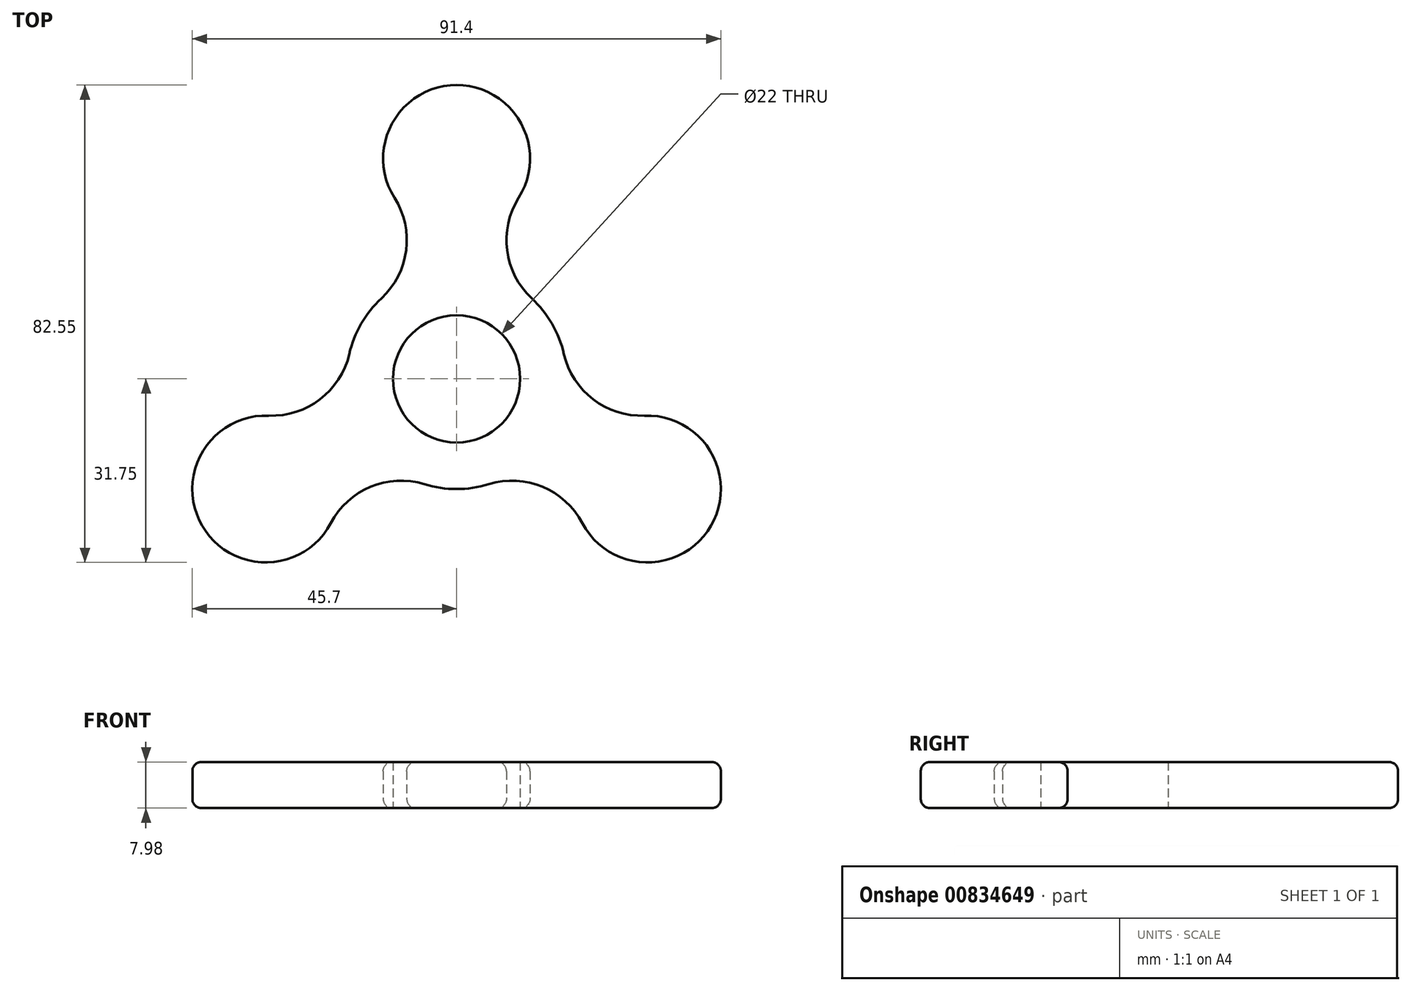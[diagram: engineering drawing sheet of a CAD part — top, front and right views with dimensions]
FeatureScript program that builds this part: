
annotation { "Feature Type Name" : "Feature", "Feature Type Description" : "" }
export const myFeature = defineFeature(function(context is Context, id is Id, definition is map)
    precondition{}
    {
        {
            var Q0;
            Q0=qCreatedBy(makeId("Top.planeOp"),FACE);
            var sketch = newSketch(context, id + "F0", { "sketchPlane" : qUnion([Q0])});
            skCircle(sketch, "E0", {"center": v(0, 0) * mm, "radius": 11 * mm});
            skLineSegment(sketch, "E1", {"start": v(0, 0) * mm, "end": v(0, 54.19) * mm, "construction": true});
            skLineSegment(sketch, "E2", {"start": v(0, 0) * mm, "end": v(61.7, 0) * mm, "construction": true});
            skCircle(sketch, "E3", {"center": v(0, 0) * mm, "radius": 19.05 * mm});
            skSolve(sketch);
        }
        {
            var Q0;
            Q0=qSketchRegion(id+"F0",true);
            extrude(context, id + "F1", {"entities" : qUnion([Q0]), "depth" : 7.98 * mm, "offsetDistance" : 25.4 * mm});
        }
        {
            var Q0;
            Q0=qCreatedBy(makeId("Top.planeOp"),FACE);
            var sketch = newSketch(context, id + "F2", { "sketchPlane" : qUnion([Q0])});
            skArc(sketch, "E4", {"start": v(10.74, 31.32) * mm, "mid": v(0, 50.8) * mm, "end": v(-10.74, 31.32) * mm});
            skArc(sketch, "E5", {"start": v(-13, 13.93) * mm, "mid": v(-8.73, 22.22) * mm, "end": v(-10.74, 31.32) * mm});
            skLineSegment(sketch, "E6", {"start": v(0, 38.1) * mm, "end": v(0, 0) * mm, "construction": true});
            skArc(sketch, "E7.MirrorCS", {"start": v(13, 13.93) * mm, "mid": v(8.73, 22.22) * mm, "end": v(10.74, 31.32) * mm});
            skLineSegment(sketch, "E8", {"start": v(-13, 13.93) * mm, "end": v(13, 13.93) * mm});
            skArc(sketch, "E9.1.0", {"start": v(-5.57, -18.22) * mm, "mid": v(-14.88, -18.68) * mm, "end": v(-21.76, -24.96) * mm});
            skLineSegment(sketch, "E9.1.1", {"start": v(-5.57, -18.22) * mm, "end": v(-18.56, 4.29) * mm});
            skArc(sketch, "E9.1.2", {"start": v(-32.5, -6.36) * mm, "mid": v(-44, -25.4) * mm, "end": v(-21.76, -24.96) * mm});
            skArc(sketch, "E9.1.3", {"start": v(-18.56, 4.29) * mm, "mid": v(-23.61, -3.55) * mm, "end": v(-32.5, -6.36) * mm});
            skArc(sketch, "E9.2.0", {"start": v(18.56, 4.29) * mm, "mid": v(23.61, -3.55) * mm, "end": v(32.5, -6.36) * mm});
            skLineSegment(sketch, "E9.2.1", {"start": v(18.56, 4.29) * mm, "end": v(5.57, -18.22) * mm});
            skArc(sketch, "E9.2.2", {"start": v(21.76, -24.96) * mm, "mid": v(44, -25.4) * mm, "end": v(32.5, -6.36) * mm});
            skArc(sketch, "E9.2.3", {"start": v(5.57, -18.22) * mm, "mid": v(14.88, -18.68) * mm, "end": v(21.76, -24.96) * mm});
            skPoint(sketch, "E9.center", {"position": v(0, 0) * mm});
            skSolve(sketch);
        }
        {
            var Q0;
            Q0 = qSketchRegion(id + "F2", true);
            extrude(context, id + "F3", {"entities" : qUnion([Q0]), "operationType" : NewBodyOperationType.ADD, "depth" : 7.98 * mm, "offsetDistance" : 25.4 * mm});
        }
        {
            var Q0;
            Q0=makeQuery(id+"F3.opExtrude","CAP_EDGE",EDGE,{"disambiguationData":[OSD([sQuery(id+"F2.wireOp",EDGE,"E9.1.0")])],"isStart":false});
            var Q1;
            Q1=makeQuery(id+"F3.opExtrude","CAP_EDGE",EDGE,{"disambiguationData":[OSD([sQuery(id+"F2.wireOp",EDGE,"E9.1.0")])],"isStart":true});
            fillet(context, id + "F4", {"entities" : qUnion([Q0, Q1]), "radius" : 1.59 * mm, "tangentPropagation" : true, "allowEdgeOverflow" : false});
        }
    });
